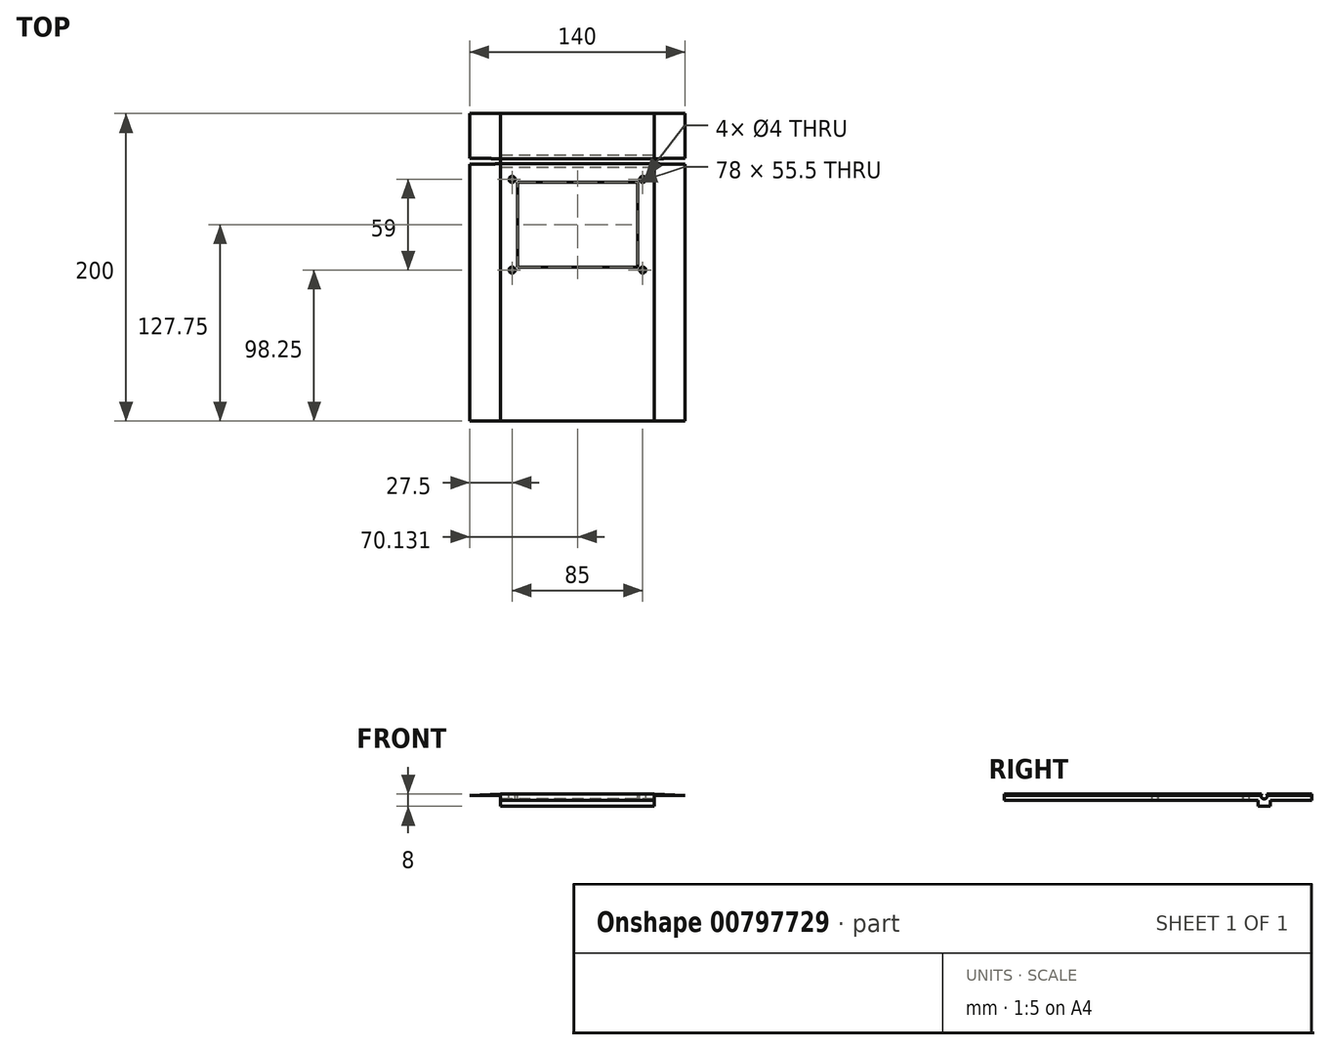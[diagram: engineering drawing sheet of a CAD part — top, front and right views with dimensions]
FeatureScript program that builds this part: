
annotation { "Feature Type Name" : "Feature", "Feature Type Description" : "" }
export const myFeature = defineFeature(function(context is Context, id is Id, definition is map)
    precondition{}
    {
        {
            var Q0;
            Q0=qCreatedBy(makeId("Top.planeOp"),FACE);
            var sketch = newSketch(context, id + "F0", { "sketchPlane" : qUnion([Q0])});
            skLineSegment(sketch, "E0", {"start": v(-45, 0) * mm, "end": v(-45, 200) * mm});
            skLineSegment(sketch, "E1", {"start": v(-45, 200) * mm, "end": v(55, 200) * mm});
            skLineSegment(sketch, "E2", {"start": v(55, 200) * mm, "end": v(55, 0) * mm});
            skLineSegment(sketch, "E3", {"start": v(55, 0) * mm, "end": v(-45, 0) * mm});
            skSolve(sketch);
        }
        {
            var Q0;
            Q0 = qSketchRegion(id + "F0", true);
            extrude(context, id + "F1", {"entities" : qUnion([Q0]), "depth" : 4 * mm, "offsetDistance" : 25 * mm});
        }
        {
            var Q0;
            Q0=makeQuery(id+"F1.opExtrude","CAP_FACE",FACE,{"disambiguationData":[OSD([sQuery(id+"F0.wireOp",EDGE,"E0"),sQuery(id+"F0.wireOp",EDGE,"E1"),sQuery(id+"F0.wireOp",EDGE,"E2"),sQuery(id+"F0.wireOp",EDGE,"E3")])],"isStart":false});
            var sketch = newSketch(context, id + "F2", { "sketchPlane" : qUnion([Q0])});
            skLineSegment(sketch, "E4.bottom", {"start": v(-33.87, 100) * mm, "end": v(44.13, 100) * mm});
            skLineSegment(sketch, "E4.top", {"start": v(-33.87, 155.5) * mm, "end": v(44.13, 155.5) * mm});
            skLineSegment(sketch, "E4.left", {"start": v(-33.87, 100) * mm, "end": v(-33.87, 155.5) * mm});
            skLineSegment(sketch, "E4.right", {"start": v(44.13, 100) * mm, "end": v(44.13, 155.5) * mm});
            skCircle(sketch, "E5", {"center": v(-37.5, 98.25) * mm, "radius": 2 * mm});
            skCircle(sketch, "E6", {"center": v(-37.5, 157.25) * mm, "radius": 2 * mm});
            skCircle(sketch, "E7", {"center": v(47.5, 157.25) * mm, "radius": 2 * mm});
            skCircle(sketch, "E8", {"center": v(47.5, 98.25) * mm, "radius": 2 * mm});
            skSolve(sketch);
        }
        {
            var Q0;
            Q0 = qSketchRegion(id + "F2", true);
            extrude(context, id + "F3", {"entities" : qUnion([Q0]), "operationType" : NewBodyOperationType.REMOVE, "oppositeDirection" : true, "depth" : 25 * mm, "offsetDistance" : 25 * mm});
        }
        {
            var Q0;
            Q0=makeQuery(id+"F1.opExtrude","SWEPT_FACE",FACE,{"disambiguationData":[OSD([sQuery(id+"F0.wireOp",EDGE,"E3")])]});
            var sketch = newSketch(context, id + "F4", { "sketchPlane" : qUnion([Q0])});
            skLineSegment(sketch, "E9", {"start": v(-45, 4) * mm, "end": v(-65, 3) * mm});
            skLineSegment(sketch, "E10", {"start": v(-65, 3) * mm, "end": v(-45, 3) * mm});
            skLineSegment(sketch, "E11", {"start": v(-45, 3) * mm, "end": v(-45, 4) * mm});
            skLineSegment(sketch, "E12", {"start": v(55, 4) * mm, "end": v(75, 3) * mm});
            skLineSegment(sketch, "E13", {"start": v(75, 3) * mm, "end": v(55, 3) * mm});
            skLineSegment(sketch, "E14", {"start": v(55, 3) * mm, "end": v(55, 4) * mm});
            skSolve(sketch);
        }
        {
            var Q0;
            Q0 = qSketchRegion(id + "F4", true);
            extrude(context, id + "F5", {"entities" : qUnion([Q0]), "operationType" : NewBodyOperationType.ADD, "oppositeDirection" : true, "depth" : 200 * mm, "offsetDistance" : 25 * mm});
        }
        {
            var Q0;
            Q0=makeQuery(id+"F1.opExtrude","CAP_FACE",FACE,{"disambiguationData":[OSD([sQuery(id+"F0.wireOp",EDGE,"E0"),sQuery(id+"F0.wireOp",EDGE,"E1"),sQuery(id+"F0.wireOp",EDGE,"E2"),sQuery(id+"F0.wireOp",EDGE,"E3")])],"isStart":true});
            var sketch = newSketch(context, id + "F6", { "sketchPlane" : qUnion([Q0])});
            skLineSegment(sketch, "E15.bottom", {"start": v(55, -165) * mm, "end": v(-45, -165) * mm});
            skLineSegment(sketch, "E15.top", {"start": v(55, -173) * mm, "end": v(-45, -173) * mm});
            skLineSegment(sketch, "E15.left", {"start": v(55, -165) * mm, "end": v(55, -173) * mm});
            skLineSegment(sketch, "E15.right", {"start": v(-45, -165) * mm, "end": v(-45, -173) * mm});
            skSolve(sketch);
        }
        {
            var Q0;
            Q0 = qSketchRegion(id + "F6", true);
            extrude(context, id + "F7", {"entities" : qUnion([Q0]), "operationType" : NewBodyOperationType.ADD, "depth" : 4 * mm, "offsetDistance" : 25 * mm});
        }
        {
            var Q0;
            Q0=makeQuery(id+"F7.boolean.opBoolean","MERGE",FACE,{"derivedFrom":[makeQuery(id+"F1.opExtrude","SWEPT_FACE",FACE,{"disambiguationData":[OSD([sQuery(id+"F0.wireOp",EDGE,"E2")])]}),makeQuery(id+"F7.opExtrude","SWEPT_FACE",FACE,{"disambiguationData":[OSD([sQuery(id+"F6.wireOp",EDGE,"E15.left")])]})]});
            var sketch = newSketch(context, id + "F8", { "sketchPlane" : qUnion([Q0])});
            skPoint(sketch, "E16.centerSnap0", {"position": v(169, -4) * mm});
            skCircle(sketch, "E17", {"center": v(169, 2.8) * mm, "radius": 2 * mm});
            skSolve(sketch);
        }
        {
            var Q0;
            Q0 = qSketchRegion(id + "F8", true);
            extrude(context, id + "F9", {"entities" : qUnion([Q0]), "operationType" : NewBodyOperationType.REMOVE, "depth" : 200 * mm, "offsetDistance" : 25 * mm, "hasSecondDirection" : true, "secondDirectionOppositeDirection" : true, "secondDirectionDepth" : 200 * mm});
        }
    });
